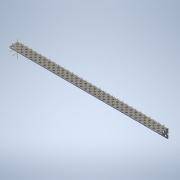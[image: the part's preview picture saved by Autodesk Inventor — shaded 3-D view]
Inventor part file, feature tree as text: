
AUTODESK INVENTOR PART (.ipt)
format: ipt  version: 2020 (Build 240168000, 168)  size: 2,392,576 bytes
history: native  units: in
note: dims shown in document units (in); Inventor stores cm internally (conversion verified against a paired STEP export)
features: other x203, pattern_linear x4, sheet_metal_op x1, extrude x1, plane x1, split x1, imported_body x1, sketch x1
ambient origin geometry x8: Origin, YZ Plane, XZ Plane, XY Plane, X Axis, Y Axis, Z Axis, Center Point
bodies: Body1 (feature_tree)
feature tree (213):
  sheet_metal_op  "Fold1"
  other  "L-Channel"
  extrude  "length cut"  Depth=0.5in
  other  "top out axis"
  other  "top inner axis"
  other  "back out axis"
  other  "back inner axis"
  pattern_linear  "top outer axes"  Count1=2 Spacing1=0.5in
  pattern_linear  "top inner axes"  Spacing1=0.5in  [1 undecoded]
  pattern_linear  "back outer axes"  Count1=2 Spacing1=0.5in
  pattern_linear  "back inner axes"  Spacing1=0.5in  [1 undecoded]
  other  "right plane"
  plane  "Work Plane3"
  split  "Split1"
  imported_body  "Base1"
  sketch  "Sketch1"  dims[d1=0.0in d4=0.5in d5=0.7874in d7=0.5in d10=0.5in d13=0.5in d14=0.7874in d16=0.5in d19=0.5in d20=-17.5in d21=0.0in d22=0.0in d23=0.0in d24=0.0in d25=0.0in d26=0.0in]
  other  "Work Point1"
  other  "Work Point2"
  other  "Work Point3"
  other  "Work Point4"
  other  "Work Axis5"
  other  "Work Axis6"
  other  "Work Axis7"
  other  "Work Axis8"
  other  "Work Axis11"
  other  "Work Axis12"
  other  "Work Axis13"
  other  "Work Axis14"
  other  "Work Axis15"
  other  "Work Axis18"
  other  "Work Axis19"
  other  "Work Axis20"
  other  "Work Axis23"
  other  "Work Axis24"
  other  "Work Axis25"
  other  "Work Axis26"
  other  "Work Axis29"
  other  "Work Axis30"
  other  "Work Axis31"
  other  "Work Axis32"
  other  "Work Axis33"
  other  "Work Axis36"
  other  "Work Axis37"
  other  "Work Axis38"
  other  "Work Axis41"
  other  "Work Axis42"
  other  "Work Axis43"
  other  "Work Axis44"
  other  "Work Axis45"
  other  "Work Axis46"
  other  "Work Axis47"
  other  "Work Axis48"
  other  "Work Axis49"
  other  "Work Axis50"
  other  "Work Axis51"
  other  "Work Axis52"
  other  "Work Axis53"
  other  "Work Axis54"
  other  "Work Axis55"
  other  "Work Axis56"
  other  "Work Axis57"
  other  "Work Axis58"
  other  "Work Axis59"
  other  "Work Axis60"
  other  "Work Axis61"
  other  "Work Axis62"
  other  "Work Axis63"
  other  "Work Axis64"
  other  "Work Axis65"
  other  "Work Axis66"
  other  "Work Axis67"
  other  "Work Axis68"
  other  "Work Axis69"
  other  "Work Axis70"
  other  "Work Axis71"
  other  "Work Axis72"
  other  "Work Axis73"
  other  "Work Axis74"
  other  "Work Axis75"
  other  "Work Axis76"
  other  "Work Axis77"
  other  "Work Axis78"
  other  "Work Axis79"
  other  "Work Axis80"
  other  "Work Axis81"
  other  "Work Axis82"
  other  "Work Axis83"
  other  "Work Axis84"
  other  "Work Axis85"
  other  "Work Axis86"
  other  "Work Axis87"
  other  "Work Axis88"
  other  "Work Axis89"
  other  "Work Axis90"
  other  "Work Axis91"
  other  "Work Axis92"
  other  "Work Axis93"
  other  "Work Axis94"
  other  "Work Axis95"
  other  "Work Axis96"
  other  "Work Axis97"
  other  "Work Axis98"
  other  "Work Axis99"
  other  "Work Axis100"
  other  "Work Axis101"
  other  "Work Axis102"
  other  "Work Axis103"
  other  "Work Axis104"
  other  "Work Axis105"
  other  "Work Axis106"
  other  "Work Axis107"
  other  "Work Axis108"
  other  "Work Axis109"
  other  "Work Axis110"
  other  "Work Axis111"
  other  "Work Axis112"
  other  "Work Axis113"
  other  "Work Axis114"
  other  "Work Axis115"
  other  "Work Axis116"
  other  "Work Axis117"
  other  "Work Axis118"
  other  "Work Axis119"
  other  "Work Axis120"
  other  "Work Axis121"
  other  "Work Axis122"
  other  "Work Axis123"
  other  "Work Axis124"
  other  "Work Axis125"
  other  "Work Axis126"
  other  "Work Axis127"
  other  "Work Axis128"
  other  "Work Axis129"
  other  "Work Axis130"
  other  "Work Axis131"
  other  "Work Axis132"
  other  "Work Axis133"
  other  "Work Axis134"
  other  "Work Axis135"
  other  "Work Axis136"
  other  "Work Axis137"
  other  "Work Axis138"
  other  "Work Axis139"
  other  "Work Axis140"
  other  "Work Axis141"
  other  "Work Axis142"
  other  "Work Axis143"
  other  "Work Axis144"
  other  "Work Axis145"
  other  "Work Axis146"
  other  "Work Axis147"
  other  "Work Axis148"
  other  "Work Axis149"
  other  "Work Axis150"
  other  "Work Axis151"
  other  "Work Axis152"
  other  "Work Axis153"
  other  "Work Axis154"
  other  "Work Axis155"
  other  "Work Axis156"
  other  "Work Axis157"
  other  "Work Axis158"
  other  "Work Axis159"
  other  "Work Axis160"
  other  "left plane"
  other  "Work Axis161"
  other  "Work Axis162"
  other  "Work Axis163"
  other  "Work Axis164"
  other  "Work Axis165"
  other  "Work Axis166"
  other  "Work Axis167"
  other  "Work Axis168"
  other  "Work Axis169"
  other  "Work Axis170"
  other  "Work Axis171"
  other  "Work Axis172"
  other  "Work Axis173"
  other  "Work Axis174"
  other  "Work Axis175"
  other  "Work Axis176"
  other  "Work Axis177"
  other  "Work Axis178"
  other  "Work Axis179"
  other  "Work Axis180"
  other  "Work Axis181"
  other  "Work Axis182"
  other  "Work Axis183"
  other  "Work Axis184"
  other  "Work Axis185"
  other  "Work Axis186"
  other  "Work Axis187"
  other  "Work Axis188"
  other  "Work Axis191"
  other  "Work Axis192"
  other  "Work Axis193"
  other  "Work Axis194"
  other  "Work Axis197"
  other  "Work Axis198"
  other  "Work Axis199"
  other  "Work Axis200"
  other  "Work Axis203"
  other  "Work Axis204"
  other  "Work Axis205"
  other  "Work Axis206"
  other  "Work Axis209"
  other  "Work Axis210"
  other  "Work Axis211"
  other  "Work Axis212"
  other  "Work Axis215"
  other  "Work Axis216"
  other  "Work Axis217"
  other  "Work Axis218"
note: 2 required parameter values undecoded (feature->parameter linkage not recoverable at this tier; creation-order binding heuristic only, values carry confidence <= 0.55)
